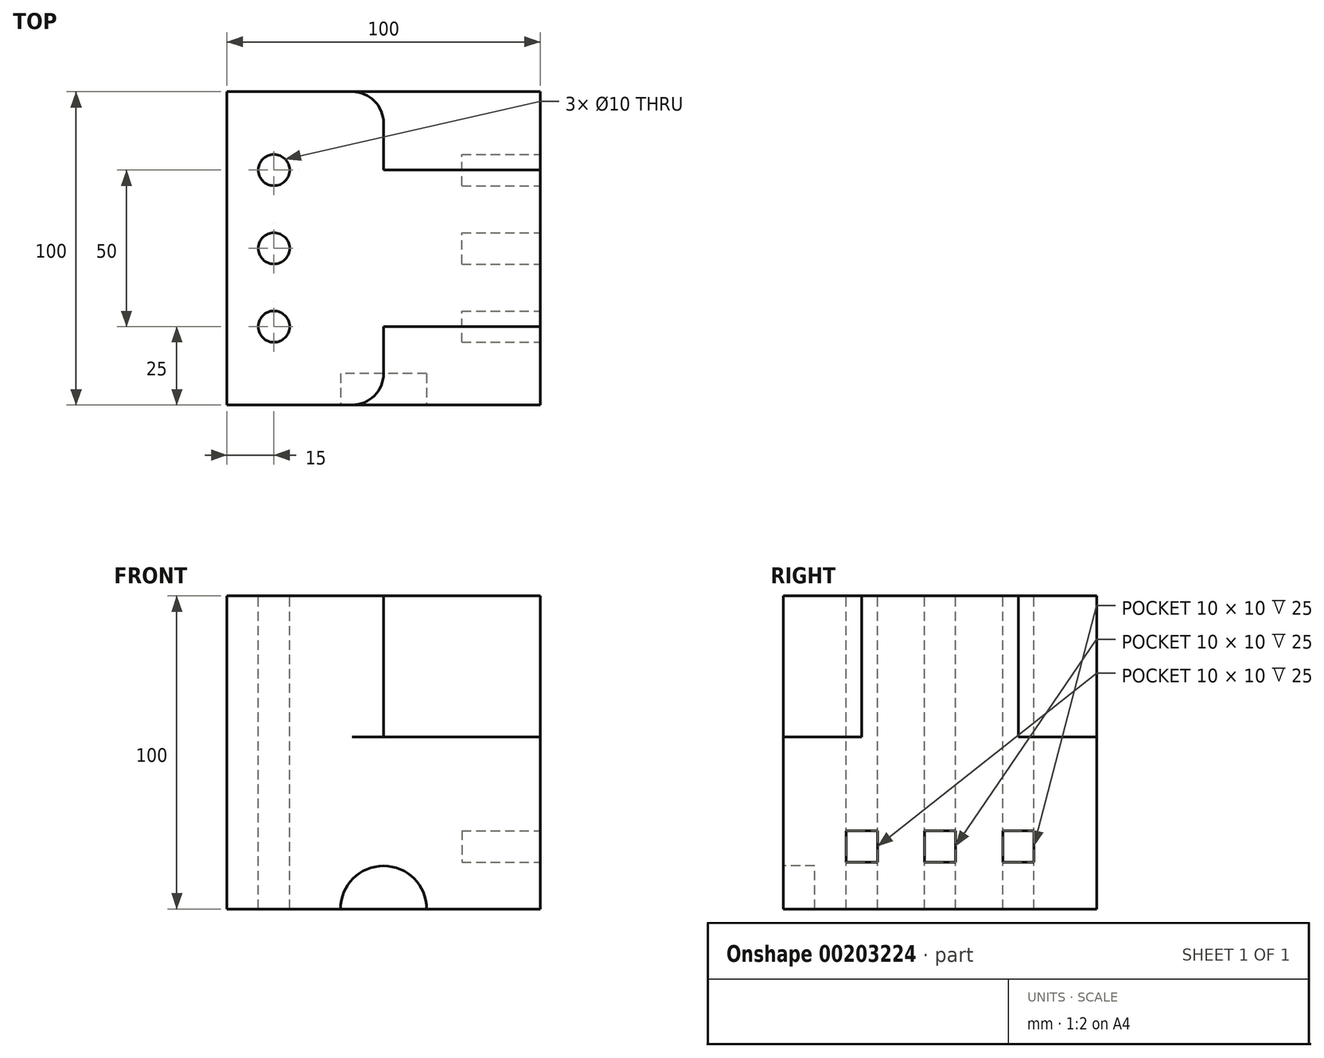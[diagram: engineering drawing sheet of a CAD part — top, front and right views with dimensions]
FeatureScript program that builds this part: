
annotation { "Feature Type Name" : "Feature", "Feature Type Description" : "" }
export const myFeature = defineFeature(function(context is Context, id is Id, definition is map)
    precondition{}
    {
        {
            var Q0;
            Q0=qCreatedBy(makeId("Right.planeOp"),FACE);
            var sketch = newSketch(context, id + "F0", { "sketchPlane" : qUnion([Q0])});
            skLineSegment(sketch, "E0", {"start": v(0, 0) * mm, "end": v(100, 0) * mm});
            skLineSegment(sketch, "E1", {"start": v(100, 0) * mm, "end": v(100, 100) * mm});
            skLineSegment(sketch, "E2", {"start": v(100, 100) * mm, "end": v(0, 100) * mm});
            skLineSegment(sketch, "E3", {"start": v(0, 100) * mm, "end": v(0, 0) * mm});
            skSolve(sketch);
        }
        {
            var Q0;
            Q0=makeQuery(id+"F0.imprint","IMPRINT",FACE,{"disambiguationData":[TD([[makeQuery(id+"F0.imprint","IMPRINT",EDGE,{"derivedFrom":sQuery(id+"F0.wireOp",EDGE,"E0")}),1.0]])]});
            extrude(context, id + "F1", {"entities" : qUnion([Q0]), "depth" : 100 * mm});
        }
        {
            var Q0;
            Q0=makeQuery(id+"F1.opExtrude","SWEPT_FACE",FACE,{"disambiguationData":[OSD([sQuery(id+"F0.wireOp",EDGE,"E2")])]});
            var sketch = newSketch(context, id + "F2", { "sketchPlane" : qUnion([Q0])});
            skLineSegment(sketch, "E4", {"start": v(49.11, 0) * mm, "end": v(100, 0) * mm});
            skLineSegment(sketch, "E5", {"start": v(100, 25) * mm, "end": v(50, 25) * mm});
            skLineSegment(sketch, "E6", {"start": v(50, 25) * mm, "end": v(50, 10) * mm});
            skLineSegment(sketch, "E7", {"start": v(40, 0) * mm, "end": v(0, 0) * mm});
            skLineSegment(sketch, "E8", {"start": v(100, 25) * mm, "end": v(100, 75) * mm});
            skLineSegment(sketch, "E9", {"start": v(100, 75) * mm, "end": v(50, 75) * mm});
            skLineSegment(sketch, "E10", {"start": v(50, 75) * mm, "end": v(50, 90) * mm});
            skLineSegment(sketch, "E11", {"start": v(40, 100) * mm, "end": v(0, 100) * mm});
            skPoint(sketch, "E12.visualSharp", {"position": v(50, 100) * mm});
            skArc(sketch, "E12.filletArc", {"start": v(50, 90) * mm, "mid": v(47.07, 97.07) * mm, "end": v(40, 100) * mm});
            skPoint(sketch, "E13.visualSharp", {"position": v(50, 0) * mm});
            skArc(sketch, "E13.filletArc", {"start": v(40, 0) * mm, "mid": v(47.07, 2.93) * mm, "end": v(50, 10) * mm});
            skCircle(sketch, "E14", {"center": v(15, 75) * mm, "radius": 5 * mm});
            skCircle(sketch, "E15", {"center": v(15, 50) * mm, "radius": 5 * mm});
            skCircle(sketch, "E16", {"center": v(15, 25) * mm, "radius": 5 * mm});
            skSolve(sketch);
        }
        {
            var Q0;
            {var subQ5=sQuery(id+"F2.wireOp",EDGE,"E9");Q0=makeQuery(id+"F2.imprint","IMPRINT",FACE,{"disambiguationData":[TD([[makeQuery(id+"F2.imprint","IMPRINT",EDGE,{"derivedFrom":subQ5}),-1.0]])]});}
            var Q1;
            {var subQ2=sQuery(id+"F2.wireOp",EDGE,"E4");Q1=makeQuery(id+"F2.imprint","IMPRINT",FACE,{"disambiguationData":[TD([[makeQuery(id+"F2.imprint","IMPRINT",EDGE,{"derivedFrom":subQ2}),-1.0]])]});}
            extrude(context, id + "F3", {"entities" : qUnion([Q0, Q1]), "operationType" : NewBodyOperationType.REMOVE, "oppositeDirection" : true, "depth" : 45 * mm});
        }
        {
            var Q0;
            Q0=makeQuery(id+"F2.imprint","IMPRINT",FACE,{"disambiguationData":[TD([[makeQuery(id+"F2.imprint","IMPRINT",EDGE,{"derivedFrom":sQuery(id+"F2.wireOp",EDGE,"E16")}),1.0]])]});
            var Q1;
            Q1=makeQuery(id+"F2.imprint","IMPRINT",FACE,{"disambiguationData":[TD([[makeQuery(id+"F2.imprint","IMPRINT",EDGE,{"derivedFrom":sQuery(id+"F2.wireOp",EDGE,"E15")}),1.0]])]});
            var Q2;
            Q2=makeQuery(id+"F2.imprint","IMPRINT",FACE,{"disambiguationData":[TD([[makeQuery(id+"F2.imprint","IMPRINT",EDGE,{"derivedFrom":sQuery(id+"F2.wireOp",EDGE,"E14")}),1.0]])]});
            var Q3;
            Q3=sQuery(id+"F2.wireOp",EDGE,"E16");
            var Q4;
            Q4=sQuery(id+"F2.wireOp",EDGE,"E15");
            var Q5;
            Q5=sQuery(id+"F2.wireOp",EDGE,"E14");
            extrude(context, id + "F4", {"entities" : qUnion([Q0, Q1, Q2]), "operationType" : NewBodyOperationType.REMOVE, "surfaceEntities" : qUnion([Q3, Q4, Q5]), "endBound" : BoundingType.THROUGH_ALL, "oppositeDirection" : true, "depth" : 25 * mm});
        }
        {
            var Q0;
            Q0=makeQuery(id+"F1.opExtrude","CAP_FACE",FACE,{"disambiguationData":[OSD([sQuery(id+"F0.wireOp",EDGE,"E0"),sQuery(id+"F0.wireOp",EDGE,"E1"),sQuery(id+"F0.wireOp",EDGE,"E2"),sQuery(id+"F0.wireOp",EDGE,"E3")])],"isStart":false});
            var sketch = newSketch(context, id + "F5", { "sketchPlane" : qUnion([Q0])});
            skLineSegment(sketch, "E17.bottom", {"start": v(20, 25) * mm, "end": v(30, 25) * mm});
            skLineSegment(sketch, "E17.top", {"start": v(20, 15) * mm, "end": v(30, 15) * mm});
            skLineSegment(sketch, "E17.left", {"start": v(20, 25) * mm, "end": v(20, 15) * mm});
            skLineSegment(sketch, "E17.right", {"start": v(30, 25) * mm, "end": v(30, 15) * mm});
            skPoint(sketch, "E17.middle", {"position": v(25, 20) * mm});
            skLineSegment(sketch, "E18.bottom", {"start": v(45, 25) * mm, "end": v(55, 25) * mm});
            skLineSegment(sketch, "E18.top", {"start": v(45, 15) * mm, "end": v(55, 15) * mm});
            skLineSegment(sketch, "E18.left", {"start": v(45, 25) * mm, "end": v(45, 15) * mm});
            skLineSegment(sketch, "E18.right", {"start": v(55, 25) * mm, "end": v(55, 15) * mm});
            skPoint(sketch, "E18.middle", {"position": v(50, 20) * mm});
            skLineSegment(sketch, "E19.bottom", {"start": v(70, 25) * mm, "end": v(80, 25) * mm});
            skLineSegment(sketch, "E19.top", {"start": v(70, 15) * mm, "end": v(80, 15) * mm});
            skLineSegment(sketch, "E19.left", {"start": v(70, 25) * mm, "end": v(70, 15) * mm});
            skLineSegment(sketch, "E19.right", {"start": v(80, 25) * mm, "end": v(80, 15) * mm});
            skPoint(sketch, "E19.middle", {"position": v(75, 20) * mm});
            skSolve(sketch);
        }
        {
            var Q0;
            Q0=makeQuery(id+"F5.imprint","IMPRINT",FACE,{"disambiguationData":[TD([[makeQuery(id+"F5.imprint","IMPRINT",EDGE,{"derivedFrom":sQuery(id+"F5.wireOp",EDGE,"E17.bottom")}),-1.0]])]});
            var Q1;
            Q1=makeQuery(id+"F5.imprint","IMPRINT",FACE,{"disambiguationData":[TD([[makeQuery(id+"F5.imprint","IMPRINT",EDGE,{"derivedFrom":sQuery(id+"F5.wireOp",EDGE,"E18.bottom")}),-1.0]])]});
            var Q2;
            Q2=makeQuery(id+"F5.imprint","IMPRINT",FACE,{"disambiguationData":[TD([[makeQuery(id+"F5.imprint","IMPRINT",EDGE,{"derivedFrom":sQuery(id+"F5.wireOp",EDGE,"E19.bottom")}),-1.0]])]});
            extrude(context, id + "F6", {"entities" : qUnion([Q0, Q1, Q2]), "operationType" : NewBodyOperationType.REMOVE, "oppositeDirection" : true, "depth" : 25 * mm});
        }
        {
            var Q0;
            Q0=makeQuery(id+"F1.opExtrude","SWEPT_FACE",FACE,{"disambiguationData":[OSD([sQuery(id+"F0.wireOp",EDGE,"E3")])]});
            var sketch = newSketch(context, id + "F7", { "sketchPlane" : qUnion([Q0])});
            skArc(sketch, "E20", {"start": v(63.75, 0) * mm, "mid": v(50, 13.75) * mm, "end": v(36.25, 0) * mm});
            skLineSegment(sketch, "E21", {"start": v(0, 0) * mm, "end": v(100, 0) * mm});
            skLineSegment(sketch, "E22", {"start": v(100, 0) * mm, "end": v(0, 0) * mm});
            skSolve(sketch);
        }
        {
            var Q0;
            {var subQ0=sQuery(id+"F7.wireOp",EDGE,"E20");Q0=makeQuery(id+"F7.imprint","IMPRINT",FACE,{"disambiguationData":[TD([[makeQuery(id+"F7.imprint","IMPRINT",EDGE,{"derivedFrom":subQ0}),1.0]])]});}
            extrude(context, id + "F8", {"entities" : qUnion([Q0]), "operationType" : NewBodyOperationType.REMOVE, "oppositeDirection" : true, "depth" : 10 * mm});
        }
    });
